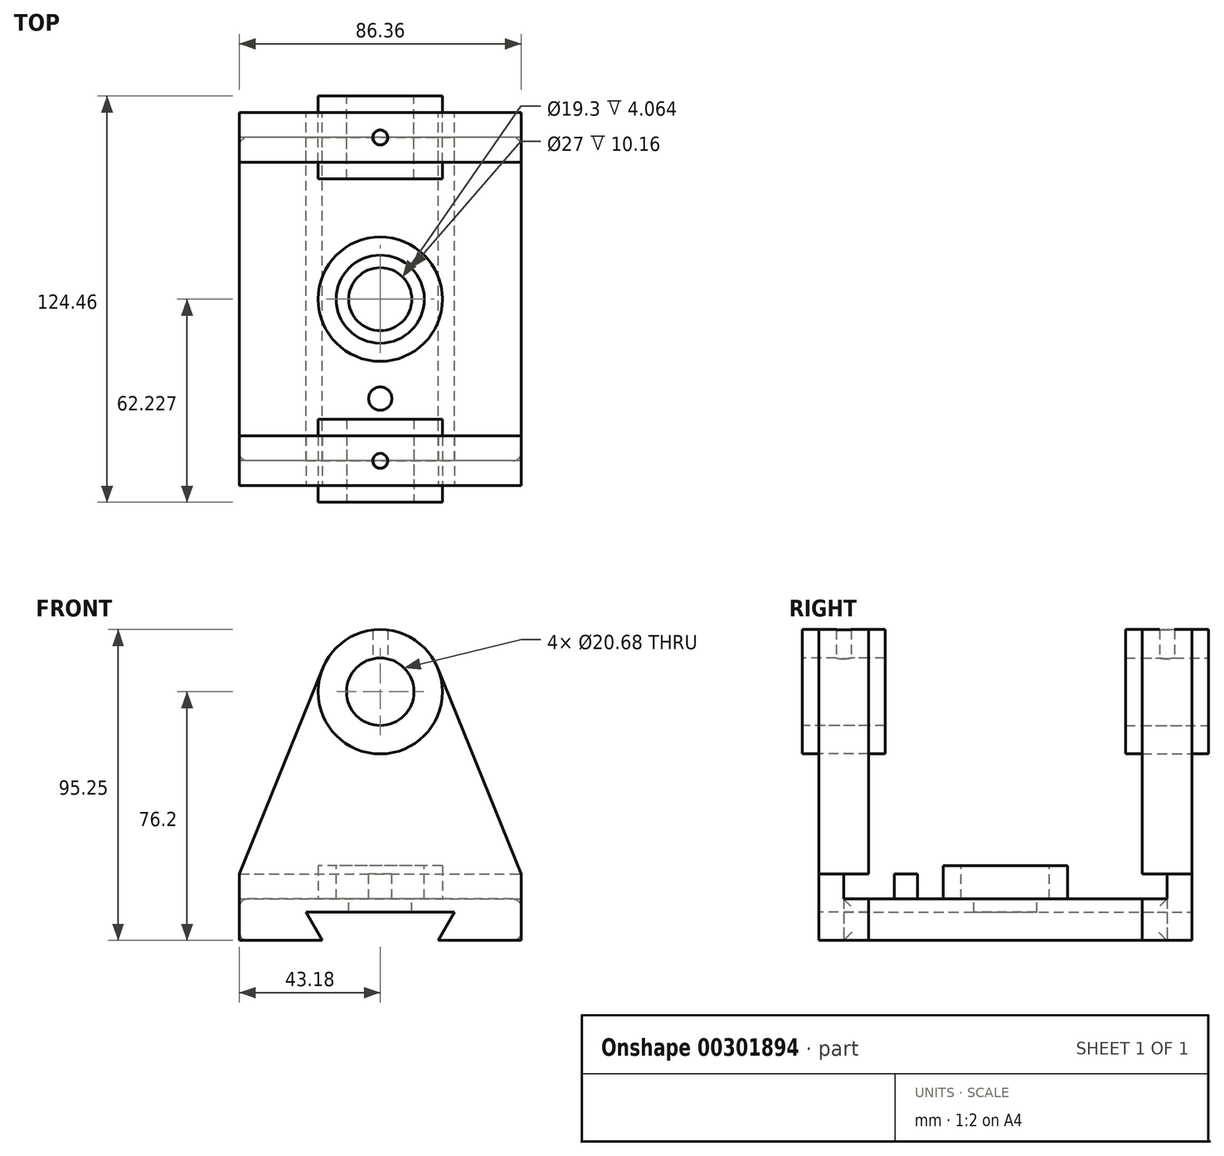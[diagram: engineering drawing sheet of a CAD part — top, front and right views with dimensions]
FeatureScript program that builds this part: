
annotation { "Feature Type Name" : "Feature", "Feature Type Description" : "" }
export const myFeature = defineFeature(function(context is Context, id is Id, definition is map)
    precondition{}
    {
        {
            var Q0;
            Q0=qCreatedBy(makeId("Front.planeOp"),FACE);
            var sketch = newSketch(context, id + "F0", { "sketchPlane" : qUnion([Q0])});
            skLineSegment(sketch, "E0.bottom", {"start": v(43.18, 10.16) * mm, "end": v(-43.18, 10.16) * mm});
            skLineSegment(sketch, "E0.top", {"start": v(43.18, -10.16) * mm, "end": v(17.78, -10.16) * mm});
            skLineSegment(sketch, "E0.left", {"start": v(43.18, 10.16) * mm, "end": v(43.18, -10.16) * mm});
            skLineSegment(sketch, "E0.right", {"start": v(-43.18, 10.16) * mm, "end": v(-43.18, -10.16) * mm});
            skPoint(sketch, "E0.middle", {"position": v(0, 0) * mm});
            skCircle(sketch, "E1", {"center": v(0, 66.04) * mm, "radius": 19.05 * mm});
            skCircle(sketch, "E2", {"center": v(0, 66.04) * mm, "radius": 10.34 * mm});
            skLineSegment(sketch, "E3", {"start": v(-43.18, 10.16) * mm, "end": v(-17.66, 73.19) * mm});
            skLineSegment(sketch, "E4", {"start": v(17.66, 73.19) * mm, "end": v(43.18, 10.16) * mm});
            skPoint(sketch, "E5.orphan", {"position": v(0, 116.8) * mm});
            skPoint(sketch, "E6.middle", {"position": v(0, -10.16) * mm});
            skLineSegment(sketch, "E7.trimOffspring", {"start": v(-17.78, -10.16) * mm, "end": v(-43.18, -10.16) * mm});
            skLineSegment(sketch, "E8", {"start": v(22.77, -1.52) * mm, "end": v(17.78, -10.16) * mm});
            skLineSegment(sketch, "E9.MirrorCS", {"start": v(-22.77, -1.52) * mm, "end": v(-17.78, -10.16) * mm});
            skLineSegment(sketch, "E10", {"start": v(-22.77, -1.52) * mm, "end": v(22.77, -1.52) * mm});
            skSolve(sketch);
        }
        {
            var Q0;
            Q0=makeQuery(id+"F0.imprint","IMPRINT",FACE,{"disambiguationData":[TD([[makeQuery(id+"F0.imprint","IMPRINT",EDGE,{"derivedFrom":sQuery(id+"F0.wireOp",EDGE,"E0.bottom")}),1.0]])]});
            var Q1;
            Q1=makeQuery(id+"F0.imprint","IMPRINT",FACE,{"disambiguationData":[TD([[makeQuery(id+"F0.imprint","IMPRINT",EDGE,{"derivedFrom":sQuery(id+"F0.wireOp",EDGE,"E2")}),-1.0]])]});
            var Q2;
            Q2=makeQuery(id+"F0.imprint","IMPRINT",FACE,{"disambiguationData":[TD([[makeQuery(id+"F0.imprint","IMPRINT",EDGE,{"derivedFrom":sQuery(id+"F0.wireOp",EDGE,"E0.bottom")}),-1.0]])]});
            extrude(context, id + "F1", {"entities" : qUnion([Q0, Q1, Q2]), "endBound" : BoundingType.SYMMETRIC, "depth" : 15.24 * mm});
        }
        {
            var Q0;
            Q0=makeQuery(id+"F0.imprint","IMPRINT",FACE,{"disambiguationData":[TD([[makeQuery(id+"F0.imprint","IMPRINT",EDGE,{"derivedFrom":sQuery(id+"F0.wireOp",EDGE,"E2")}),-1.0]])]});
            extrude(context, id + "F2", {"entities" : qUnion([Q0]), "endBound" : BoundingType.SYMMETRIC, "depth" : 25.4 * mm});
        }
        {
            var Q0;
            Q0=qCreatedBy(makeId("Top.planeOp"),FACE);
            var sketch = newSketch(context, id + "F3", { "sketchPlane" : qUnion([Q0])});
            skCircle(sketch, "E11", {"center": v(0, 0) * mm, "radius": 2.29 * mm});
            skSolve(sketch);
        }
        {
            var Q0;
            Q0=makeQuery(id+"F3.imprint","IMPRINT",FACE,{"disambiguationData":[TD([[makeQuery(id+"F3.imprint","IMPRINT",EDGE,{"derivedFrom":sQuery(id+"F3.wireOp",EDGE,"E11")}),1.0]])]});
            extrude(context, id + "F4", {"entities" : qUnion([Q0]), "operationType" : NewBodyOperationType.REMOVE, "depth" : 98.8 * mm, "hasSecondDirection" : true, "secondDirectionOppositeDirection" : false, "secondDirectionDepth" : 69.34 * mm});
        }
        {
            var Q0;
            Q0=qCreatedBy(makeId("Front.planeOp"),FACE);
            cPlane(context, id + "F5", {"entities" : qUnion([Q0]), "cplaneType" : CPlaneType.OFFSET, "offset" : 49.53 * mm, "width" : 152.4 * mm, "height" : 152.4 * mm});
        }
        {
            var Q0;
            Q0=makeQuery(id+"F2.opExtrude","SWEPT_BODY",BODY,{"disambiguationData":[OSD([sQuery(id+"F0.wireOp",EDGE,"E1"),sQuery(id+"F0.wireOp",EDGE,"E2")])]});
            var Q1;
            Q1=makeQuery(id+"F1.opExtrude","SWEPT_BODY",BODY,{"disambiguationData":[OSD([sQuery(id+"F0.wireOp",EDGE,"E0.top"),sQuery(id+"F0.wireOp",EDGE,"E0.left"),sQuery(id+"F0.wireOp",EDGE,"E0.right"),sQuery(id+"F0.wireOp",EDGE,"E1"),sQuery(id+"F0.wireOp",EDGE,"E2"),sQuery(id+"F0.wireOp",EDGE,"E3"),sQuery(id+"F0.wireOp",EDGE,"E4"),sQuery(id+"F0.wireOp",EDGE,"E7.trimOffspring"),sQuery(id+"F0.wireOp",EDGE,"E8"),sQuery(id+"F0.wireOp",EDGE,"E9.MirrorCS"),sQuery(id+"F0.wireOp",EDGE,"E10")])]});
            var Q2;
            Q2=qCreatedBy(id+"F5.planeOp",FACE);
            mirror(context, id + "F6", {"entities" : qUnion([Q0, Q1]), "mirrorPlane" : qUnion([Q2])});
        }
        {
            var Q0;
            Q0=makeQuery(id+"F0.imprint","IMPRINT",FACE,{"disambiguationData":[TD([[makeQuery(id+"F0.imprint","IMPRINT",EDGE,{"derivedFrom":sQuery(id+"F0.wireOp",EDGE,"E0.bottom")}),1.0]])]});
            extrude(context, id + "F7", {"entities" : qUnion([Q0]), "depth" : 99.06 * mm});
        }
        {
            var Q0;
            Q0=makeQuery(id+"F7.opExtrude","SWEPT_FACE",FACE,{"disambiguationData":[OSD([sQuery(id+"F0.wireOp",EDGE,"E0.bottom")])]});
            var sketch = newSketch(context, id + "F8", { "sketchPlane" : qUnion([Q0])});
            skCircle(sketch, "E12", {"center": v(0, -49.53) * mm, "radius": 19.05 * mm});
            skCircle(sketch, "E13", {"center": v(0, -49.53) * mm, "radius": 13.5 * mm});
            skCircle(sketch, "E14", {"center": v(0, -49.53) * mm, "radius": 9.65 * mm});
            skCircle(sketch, "E15", {"center": v(0, -19.05) * mm, "radius": 3.56 * mm});
            skCircle(sketch, "E16.MirrorC", {"center": v(0, -80) * mm, "radius": 3.56 * mm});
            skSolve(sketch);
        }
        {
            var Q0;
            Q0=makeQuery(id+"F8.imprint","IMPRINT",FACE,{"disambiguationData":[TD([[makeQuery(id+"F8.imprint","IMPRINT",EDGE,{"derivedFrom":sQuery(id+"F8.wireOp",EDGE,"E14")}),1.0]])]});
            extrude(context, id + "F9", {"entities" : qUnion([Q0]), "operationType" : NewBodyOperationType.REMOVE, "oppositeDirection" : true, "depth" : 25.4 * mm});
        }
        {
            var Q0;
            Q0=makeQuery(id+"F8.imprint","IMPRINT",FACE,{"disambiguationData":[TD([[makeQuery(id+"F8.imprint","IMPRINT",EDGE,{"derivedFrom":sQuery(id+"F8.wireOp",EDGE,"E13")}),1.0]])]});
            extrude(context, id + "F10", {"entities" : qUnion([Q0]), "operationType" : NewBodyOperationType.REMOVE, "oppositeDirection" : true, "depth" : 7.62 * mm});
        }
        {
            var Q0;
            Q0=makeQuery(id+"F8.imprint","IMPRINT",FACE,{"disambiguationData":[TD([[makeQuery(id+"F8.imprint","IMPRINT",EDGE,{"derivedFrom":sQuery(id+"F8.wireOp",EDGE,"E12")}),1.0]])]});
            extrude(context, id + "F11", {"entities" : qUnion([Q0]), "operationType" : NewBodyOperationType.ADD, "depth" : 2.54 * mm});
        }
        {
            var Q0;
            Q0=makeQuery(id+"F8.imprint","IMPRINT",FACE,{"disambiguationData":[TD([[makeQuery(id+"F8.imprint","IMPRINT",EDGE,{"derivedFrom":sQuery(id+"F8.wireOp",EDGE,"E16.MirrorC")}),-1.0]])]});
            var Q1;
            Q1=makeQuery(id+"F8.imprint","IMPRINT",FACE,{"disambiguationData":[TD([[makeQuery(id+"F8.imprint","IMPRINT",EDGE,{"derivedFrom":sQuery(id+"F8.wireOp",EDGE,"E15")}),1.0]])]});
            extrude(context, id + "F12", {"entities" : qUnion([Q0, Q1]), "operationType" : NewBodyOperationType.REMOVE, "oppositeDirection" : true, "depth" : 7.62 * mm});
        }
        {
            var Q0;
            Q0=makeQuery(id+"F6.opPattern","COPY",FACE,{"derivedFrom":makeQuery(id+"F1.opExtrude","SWEPT_FACE",FACE,{"disambiguationData":[OSD([sQuery(id+"F0.wireOp",EDGE,"E4")])]}),"instanceName":"1"});
            var Q1;
            Q1=makeQuery(id+"F1.opExtrude","SWEPT_FACE",FACE,{"disambiguationData":[OSD([sQuery(id+"F0.wireOp",EDGE,"E4")])]});
            var Q2;
            Q2=makeQuery(id+"F6.opPattern","COPY",FACE,{"derivedFrom":makeQuery(id+"F1.opExtrude","SWEPT_FACE",FACE,{"disambiguationData":[OSD([sQuery(id+"F0.wireOp",EDGE,"E0.left")])]}),"instanceName":"1"});
            var Q3;
            Q3=makeQuery(id+"F1.opExtrude","SWEPT_FACE",FACE,{"disambiguationData":[OSD([sQuery(id+"F0.wireOp",EDGE,"E0.left")])]});
            var Q4;
            Q4=makeQuery(id+"F7.opExtrude","SWEPT_FACE",FACE,{"disambiguationData":[OSD([sQuery(id+"F0.wireOp",EDGE,"E0.left")])]});
            var Q5;
            Q5=makeQuery(id+"F6.opPattern","COPY",FACE,{"derivedFrom":makeQuery(id+"F1.opExtrude","SWEPT_FACE",FACE,{"disambiguationData":[OSD([sQuery(id+"F0.wireOp",EDGE,"E0.right")])]}),"instanceName":"1"});
            var Q6;
            Q6=makeQuery(id+"F7.opExtrude","SWEPT_FACE",FACE,{"disambiguationData":[OSD([sQuery(id+"F0.wireOp",EDGE,"E0.right")])]});
            var Q7;
            Q7=makeQuery(id+"F1.opExtrude","SWEPT_FACE",FACE,{"disambiguationData":[OSD([sQuery(id+"F0.wireOp",EDGE,"E0.right")])]});
            fillet(context, id + "F13", {"entities" : qUnion([Q0, Q1, Q2, Q3, Q4, Q5, Q6, Q7]), "radius" : 2.54 * mm, "tangentPropagation" : true, "allowEdgeOverflow" : false});
        }
    });
